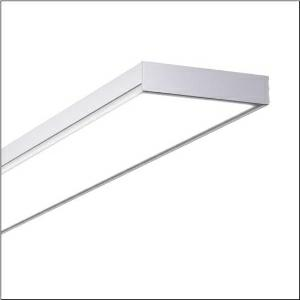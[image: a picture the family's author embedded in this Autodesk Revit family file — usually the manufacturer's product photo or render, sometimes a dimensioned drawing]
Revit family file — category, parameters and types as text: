
# Revit family: apollon_r__31_surface_51mp25wd2441e_f457
name_source: partatom
category: Lighting Fixtures
units: mm (PartAtom-declared; Revit-internal decimal feet)

## family parameters
Cut with Voids When Loaded = No
Host = Face
Light Source = No
Part Type = Normal
Room Calculation Point = No
Round Connector Dimension = Use Diameter
Shared = No

## types (1)
- Apollon® 31 Surface (1 x LED, 3800 lm, 28 W, 4000K)
    Apparent Load = 28 VA
    CIE Flux Codes = 61 87 97 97 100
    Color Rendering = 80
    Color Temperature = 4000K
    Default Elevation = 1800 mm
    Description = Apollon® 31 Surface, office luminaire, primary optical cover: micro prismatic cover, of PMMA, light emission: direct distribution, primary light characteristic: symmetric, installation type: surface-mounted, LED, rated luminous flux: 3.800lm, luminous efficacy: 134lm/W, light colour: 840, colour temperature: 4000K, control gear: DALI 2, with terminal, 5-pole, mains connection: 220..240V, AC, 50/60Hz, rated input power: 28W, housing, of sheet steel, coil coated, metallic grey (RAL 9006), length: 1.245mm, width: 200mm, height: 44mm, protection rating (complete): IP20, insulation class (complete): insulation class II (safety insulation), certification: CE, impact resistance: IK02, permissible operating ambient temperature: -20..+40°C, standard: EN 60598-2-22, packaging unit: 1 piece
    Height = 44 mm
    Lamp = 1 x LED
    Lamp Light Flux = 3800 lm
    Lamp Power = 28 W
    Lamp count = 1
    Length = 1245 mm
    Luminous efficacy = 136 lm/W
    Manufacturer = Siteco
    ModVariant = No
    Model = 51MP25WD2441E
    Mounting Place = Ceiling
    Mounting Type = Surface mounted
    Number of Poles = 1
    OnlyDefault = Yes
    Power Factor = 1
    Product Name = Apollon® 31 Surface
    Product group = office luminaire | ceiling mounted
    ProductGroupID = 302
    Protection Class = Protection class II
    Protection Degree = IP 20
    RLX_Detail_Level = 1
    RLX_Emergency_Light_Flux = 0 lm
    RLX_Emergency_Type = 0
    RLX_Emergency_Type_DB = No
    RlxData = <blob elided: 24097 chars, md5=3d65a891>
    Socket = socket
    Standby Power = 0 W
    System Light Flux = 3800 lm
    System Power = 28 W
    Type Comments = Product without accessories
    Type Image = l_1313654.jpg
    URL = http://relux.com
    VarID = ---
    Voltage = 0 V
    Weight = 0.00 kg
    Width = 200 mm  [stored 0.656168 ft]

note: [stored X ft] marks values corroborated as IEEE doubles in the binary element streams (Revit-internal decimal feet)

## geometry (parser evidence)
native form markers: Blend x4, Sweep x11
no freeform markers — native parametric forms only
